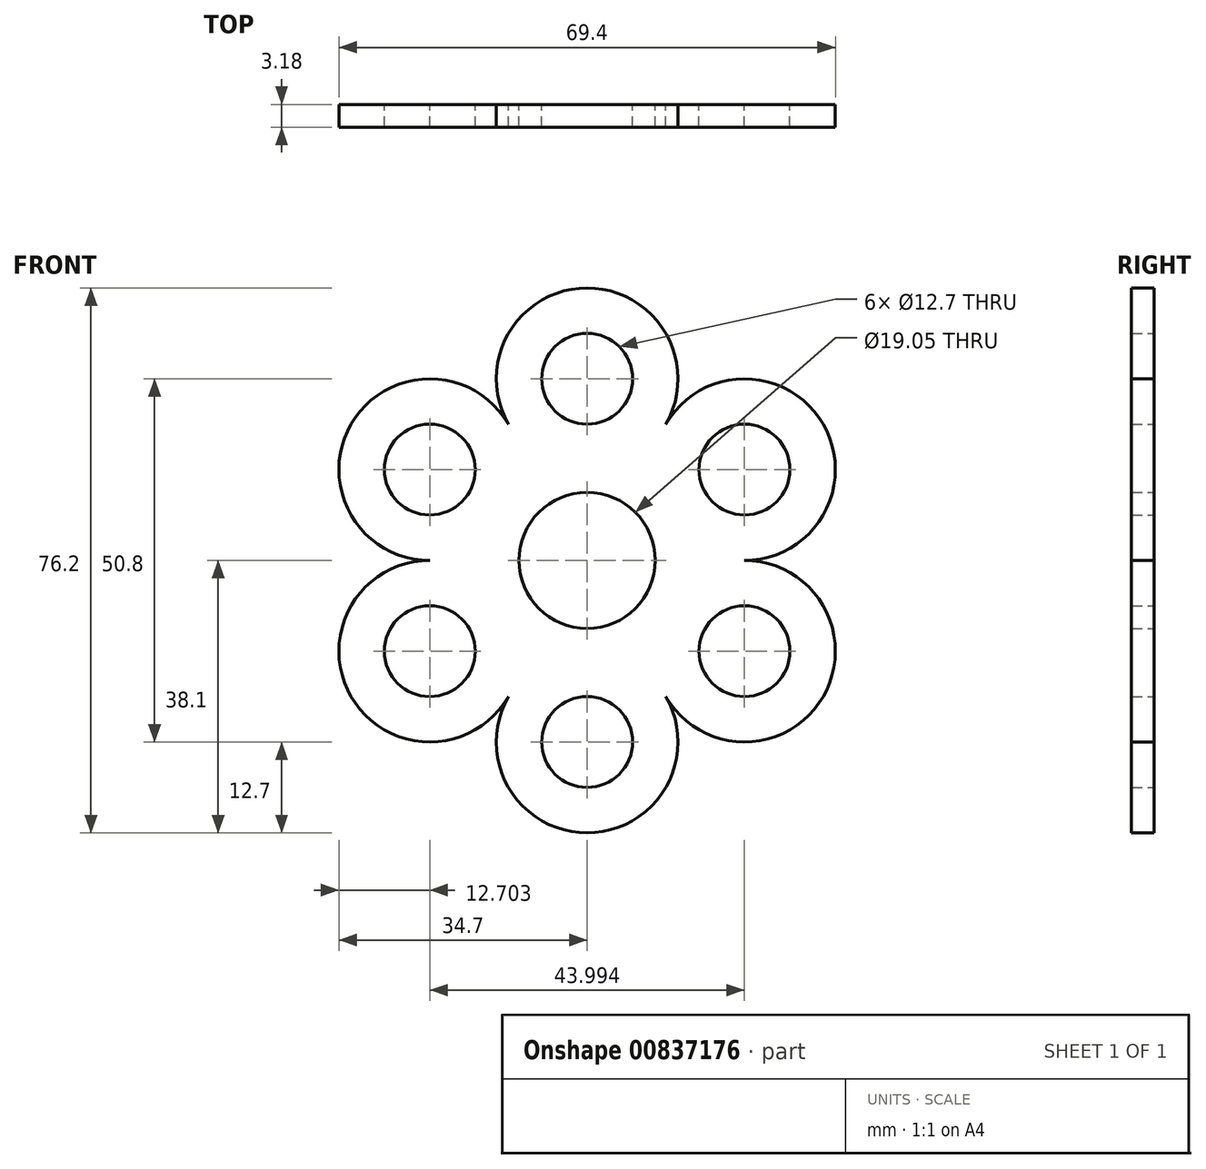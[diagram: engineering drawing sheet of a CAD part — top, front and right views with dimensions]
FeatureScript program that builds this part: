
annotation { "Feature Type Name" : "Feature", "Feature Type Description" : "" }
export const myFeature = defineFeature(function(context is Context, id is Id, definition is map)
    precondition{}
    {
        {
            var Q0;
            Q0=qCreatedBy(makeId("Front.planeOp"),FACE);
            var sketch = newSketch(context, id + "F0", { "sketchPlane" : qUnion([Q0])});
            skCircle(sketch, "E0", {"center": v(0, 0) * mm, "radius": 9.53 * mm});
            skLineSegment(sketch, "E1", {"start": v(0, 34.42) * mm, "end": v(0, -40.51) * mm, "construction": true});
            skLineSegment(sketch, "E2", {"start": v(0, 0) * mm, "end": v(36.38, -21) * mm, "construction": true});
            skLineSegment(sketch, "E3", {"start": v(0, 0) * mm, "end": v(-34.07, -19.67) * mm, "construction": true});
            skLineSegment(sketch, "E4", {"start": v(0, 0) * mm, "end": v(-36.83, 21.27) * mm, "construction": true});
            skLineSegment(sketch, "E5", {"start": v(0, 0) * mm, "end": v(37.18, 21.46) * mm, "construction": true});
            skCircle(sketch, "E6", {"center": v(22, 12.7) * mm, "radius": 6.35 * mm});
            skCircle(sketch, "E7", {"center": v(22, -12.7) * mm, "radius": 6.35 * mm});
            skCircle(sketch, "E8", {"center": v(0, -25.4) * mm, "radius": 6.35 * mm});
            skCircle(sketch, "E9", {"center": v(-22, -12.7) * mm, "radius": 6.35 * mm});
            skCircle(sketch, "E10", {"center": v(-22, 12.7) * mm, "radius": 6.35 * mm});
            skCircle(sketch, "E11", {"center": v(0, 25.4) * mm, "radius": 6.35 * mm});
            skLineSegment(sketch, "E12", {"start": v(0, -12.7) * mm, "end": v(0, -12.7) * mm});
            skLineSegment(sketch, "E13", {"start": v(0, 25.4) * mm, "end": v(22, 12.7) * mm, "construction": true});
            skLineSegment(sketch, "E14", {"start": v(22, 12.7) * mm, "end": v(22, -12.7) * mm, "construction": true});
            skLineSegment(sketch, "E15", {"start": v(22, -12.7) * mm, "end": v(0, -25.4) * mm, "construction": true});
            skLineSegment(sketch, "E16", {"start": v(0, -25.4) * mm, "end": v(-22, -12.7) * mm, "construction": true});
            skLineSegment(sketch, "E17", {"start": v(-22, -12.7) * mm, "end": v(-22, 12.7) * mm, "construction": true});
            skLineSegment(sketch, "E18", {"start": v(-22, 12.7) * mm, "end": v(0, 25.4) * mm, "construction": true});
            skArc(sketch, "E19", {"start": v(11, 19.05) * mm, "mid": v(0, 38.1) * mm, "end": v(-11, 19.05) * mm});
            skArc(sketch, "E20", {"start": v(-11, 19.05) * mm, "mid": v(-33, 19.05) * mm, "end": v(-22, 0) * mm});
            skArc(sketch, "E21", {"start": v(-22, 0) * mm, "mid": v(-33, -19.05) * mm, "end": v(-11, -19.05) * mm});
            skArc(sketch, "E22", {"start": v(-11, -19.05) * mm, "mid": v(0, -38.1) * mm, "end": v(11, -19.05) * mm});
            skArc(sketch, "E23", {"start": v(11, -19.05) * mm, "mid": v(33, -19.05) * mm, "end": v(22, 0) * mm});
            skArc(sketch, "E24", {"start": v(22, 0) * mm, "mid": v(33, 19.05) * mm, "end": v(11, 19.05) * mm});
            skSolve(sketch);
        }
        {
            var Q0;
            Q0=makeQuery(id+"F0.imprint","IMPRINT",FACE,{"disambiguationData":[TD([[makeQuery(id+"F0.imprint","IMPRINT",EDGE,{"derivedFrom":sQuery(id+"F0.wireOp",EDGE,"E0")}),-1.0]])]});
            extrude(context, id + "F1", {"entities" : qUnion([Q0]), "depth" : 3.17 * mm, "offsetDistance" : 25.4 * mm});
        }
    });
